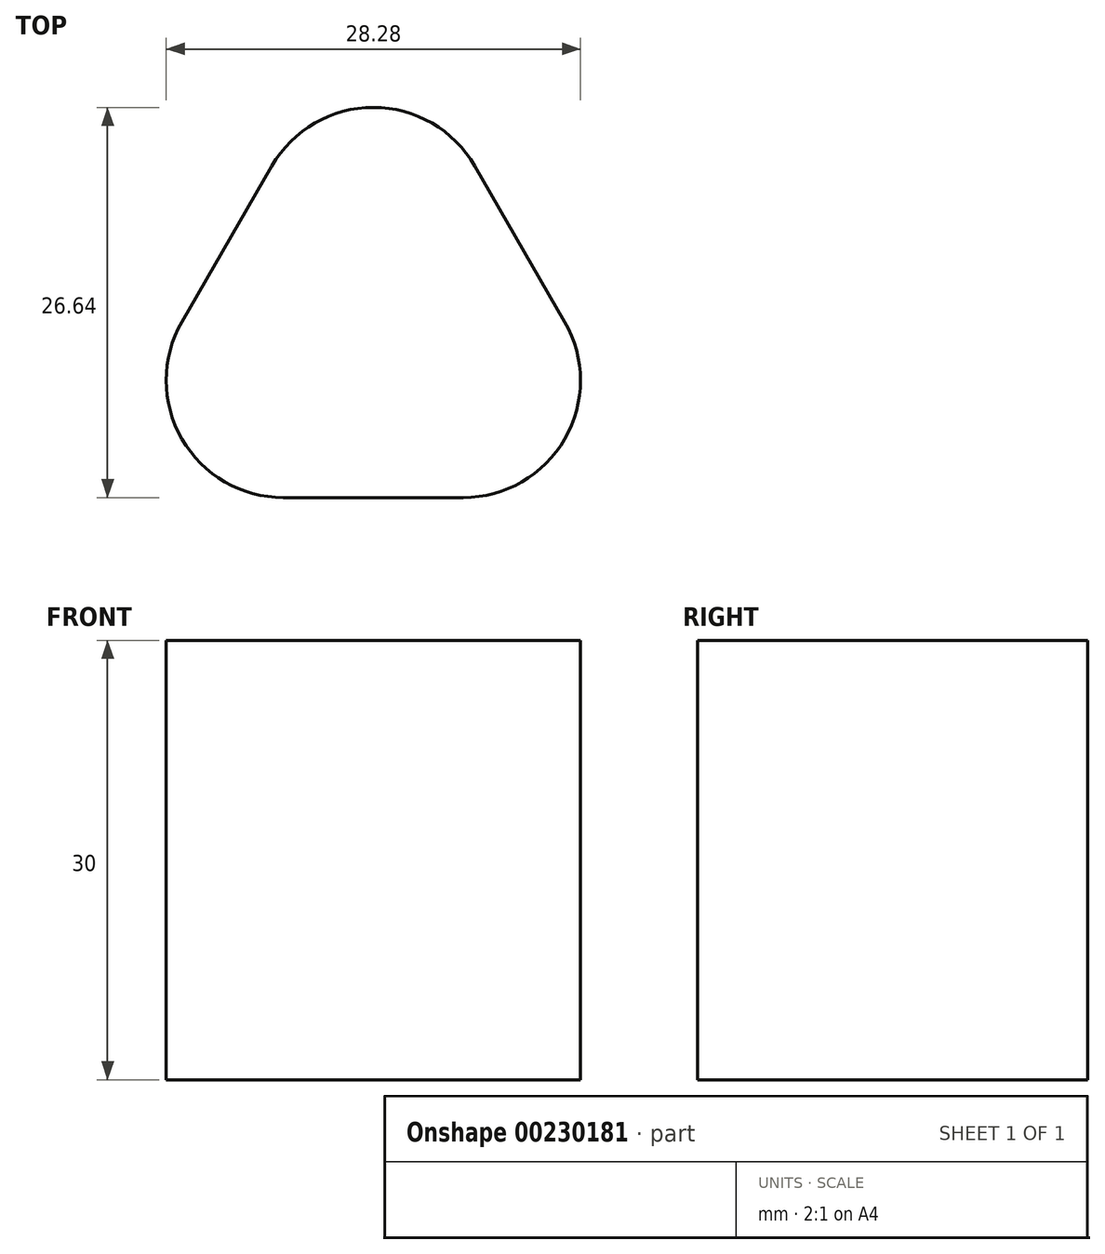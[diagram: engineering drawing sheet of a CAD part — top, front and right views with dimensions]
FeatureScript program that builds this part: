
annotation { "Feature Type Name" : "Feature", "Feature Type Description" : "" }
export const myFeature = defineFeature(function(context is Context, id is Id, definition is map)
    precondition{}
    {
        {
            var Q0;
            Q0=qCreatedBy(makeId("Top.planeOp"),FACE);
            var sketch = newSketch(context, id + "F0", { "sketchPlane" : qUnion([Q0])});
            skLineSegment(sketch, "E0", {"start": v(0, 0) * mm, "end": v(6.14, 0) * mm});
            skLineSegment(sketch, "E1", {"start": v(13.07, 12) * mm, "end": v(6.93, 22.64) * mm});
            skLineSegment(sketch, "E2", {"start": v(-6.93, 22.64) * mm, "end": v(-13.07, 12) * mm});
            skLineSegment(sketch, "E3", {"start": v(-6.14, 0) * mm, "end": v(0, 0) * mm});
            skPoint(sketch, "E4.visualSharp", {"position": v(0, 34.64) * mm});
            skArc(sketch, "E4.filletArc", {"start": v(6.93, 22.64) * mm, "mid": v(0, 26.64) * mm, "end": v(-6.93, 22.64) * mm});
            skPoint(sketch, "E5.visualSharp", {"position": v(-20, 0) * mm});
            skArc(sketch, "E5.filletArc", {"start": v(-13.07, 12) * mm, "mid": v(-13.07, 4) * mm, "end": v(-6.14, 0) * mm});
            skPoint(sketch, "E6.visualSharp", {"position": v(20, 0) * mm});
            skArc(sketch, "E6.filletArc", {"start": v(6.14, 0) * mm, "mid": v(13.07, 4) * mm, "end": v(13.07, 12) * mm});
            skSolve(sketch);
        }
        {
            var Q0;
            Q0=qSketchRegion(id+"F0",true);
            extrude(context, id + "F1", {"entities" : qUnion([Q0]), "depth" : 30 * mm});
        }
    });
